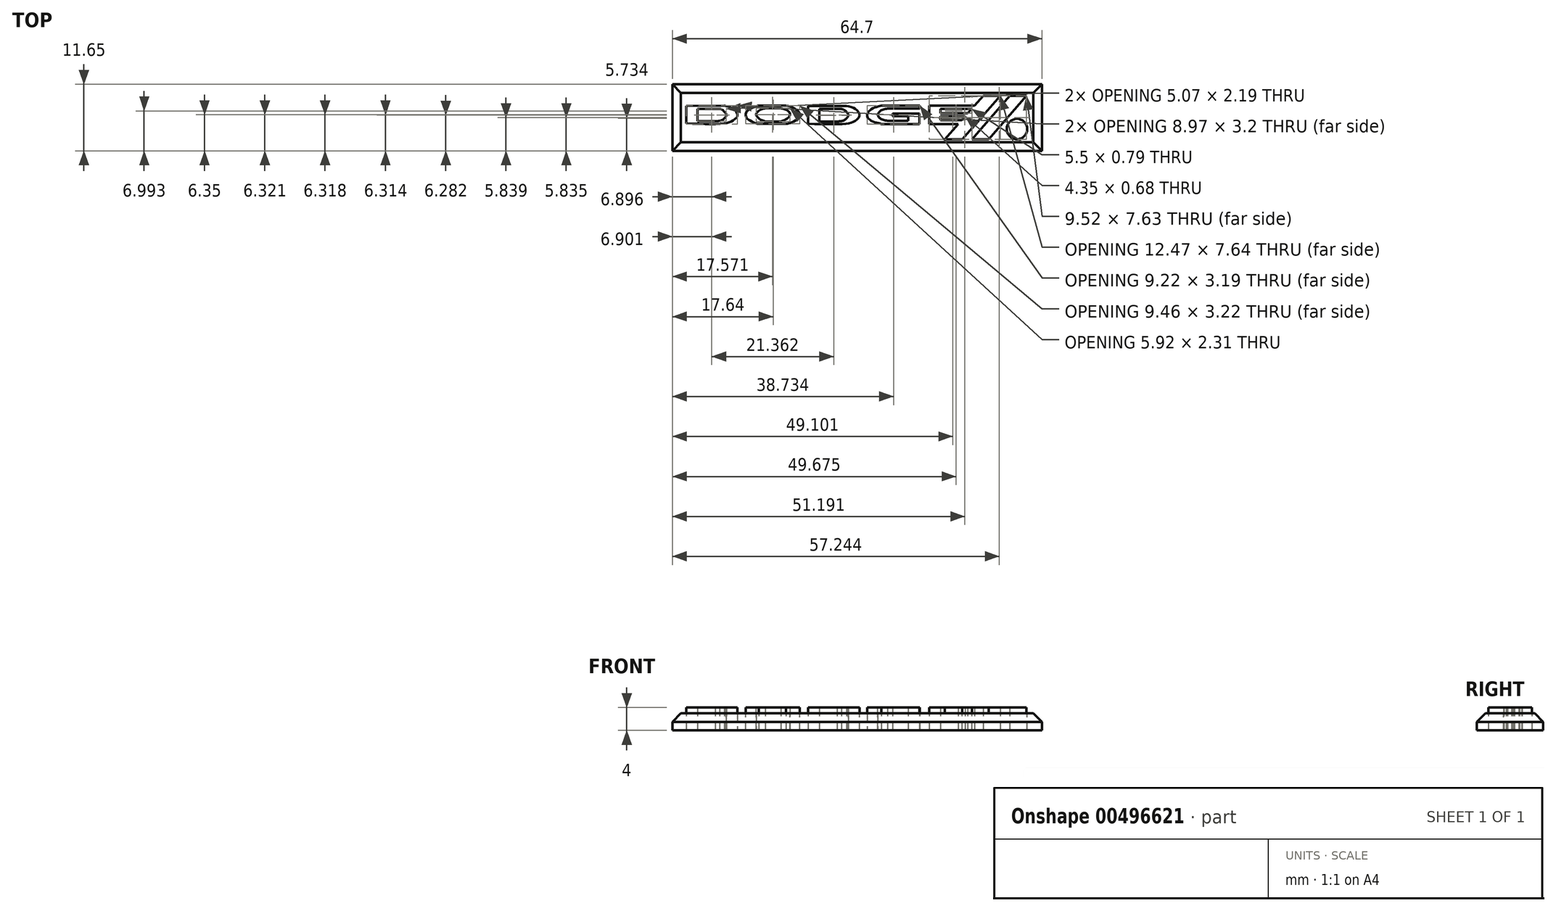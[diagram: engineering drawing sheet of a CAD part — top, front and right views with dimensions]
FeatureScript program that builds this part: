
annotation { "Feature Type Name" : "Feature", "Feature Type Description" : "" }
export const myFeature = defineFeature(function(context is Context, id is Id, definition is map)
    precondition{}
    {
        {
            var Q0;
            Q0=qCreatedBy(makeId("Top.planeOp"),FACE);
            var sketch = newSketch(context, id + "F0", { "sketchPlane" : qUnion([Q0])});
            skFitSpline(sketch, "E0", {"points": [v(0, 16.66) * mm, v(0, 13.55) * mm], "startDerivative": vector(0, -3.11) * mm, "endDerivative": vector(0, -3.11) * mm});
            skFitSpline(sketch, "E1", {"points": [v(0, 13.55) * mm, v(6.62, 13.55) * mm, v(7.96, 13.93) * mm, v(8.8, 14.55) * mm, v(8.99, 15.03) * mm, v(8.8, 15.64) * mm, v(7.95, 16.33) * mm, v(6.72, 16.67) * mm], "startDerivative": vector(26.01, -0.73) * mm, "endDerivative": vector(-9.52, 1.84) * mm});
            skFitSpline(sketch, "E2", {"points": [v(0, 16.66) * mm, v(6.72, 16.67) * mm], "startDerivative": vector(6.72, 0.01) * mm, "endDerivative": vector(6.72, 0.01) * mm});
            skFitSpline(sketch, "E3", {"points": [v(7.03, 15.1) * mm, v(7.03, 14.9) * mm, v(6.86, 14.67) * mm, v(6.62, 14.4) * mm, v(6.26, 14.16) * mm, v(5.72, 14) * mm, v(5.07, 13.95) * mm], "startDerivative": vector(0.28, -1.77) * mm, "endDerivative": vector(-3.12, -0.14) * mm});
            skFitSpline(sketch, "E4", {"points": [v(5.07, 13.95) * mm, v(1.96, 13.95) * mm], "startDerivative": vector(-3.11, 0) * mm, "endDerivative": vector(-3.11, 0) * mm});
            skFitSpline(sketch, "E5", {"points": [v(1.96, 13.95) * mm, v(1.96, 16.14) * mm], "startDerivative": vector(0, 2.2) * mm, "endDerivative": vector(0, 2.2) * mm});
            skFitSpline(sketch, "E6", {"points": [v(1.96, 16.14) * mm, v(5.86, 16.14) * mm], "startDerivative": vector(3.71, 0) * mm, "endDerivative": vector(3.71, 0) * mm});
            skFitSpline(sketch, "E7", {"points": [v(7.03, 15.1) * mm, v(7.03, 15.22) * mm, v(6.85, 15.48) * mm, v(6.52, 15.82) * mm, v(6.27, 16.01) * mm, v(5.86, 16.14) * mm], "startDerivative": vector(0.15, 0.9) * mm, "endDerivative": vector(-1.9, 0.46) * mm});
            skFitSpline(sketch, "E8", {"points": [v(15.1, 16.23) * mm, v(16.58, 16.22) * mm], "startDerivative": vector(1.48, 0) * mm, "endDerivative": vector(1.48, 0) * mm});
            skFitSpline(sketch, "E9", {"points": [v(16.58, 16.22) * mm, v(16.93, 16.15) * mm, v(17.61, 15.92) * mm, v(18.12, 15.42) * mm, v(18.19, 15.1) * mm, v(18.1, 14.87) * mm, v(17.67, 14.41) * mm, v(16.93, 14.06) * mm, v(16.58, 13.92) * mm], "startDerivative": vector(3.04, -0.61) * mm, "endDerivative": vector(-2.9, -1.12) * mm});
            skFitSpline(sketch, "E10", {"points": [v(15.1, 16.23) * mm, v(13.89, 16.23) * mm], "startDerivative": vector(-1.2, 0) * mm, "endDerivative": vector(-1.2, 0) * mm});
            skFitSpline(sketch, "E11", {"points": [v(13.89, 16.23) * mm, v(13.5, 16.14) * mm, v(12.9, 15.92) * mm, v(12.39, 15.49) * mm, v(12.27, 15.17) * mm, v(12.4, 14.83) * mm, v(12.88, 14.35) * mm, v(13.47, 14.07) * mm, v(13.89, 13.92) * mm], "startDerivative": vector(-3.28, -0.73) * mm, "endDerivative": vector(3.41, -1.16) * mm});
            skFitSpline(sketch, "E12", {"points": [v(13.89, 13.92) * mm, v(16.58, 13.92) * mm], "startDerivative": vector(2.69, 0) * mm, "endDerivative": vector(2.69, 0) * mm});
            skFitSpline(sketch, "E13", {"points": [v(15.1, 16.72) * mm, v(17.5, 16.72) * mm], "startDerivative": vector(2.4, 0) * mm, "endDerivative": vector(2.4, 0) * mm});
            skFitSpline(sketch, "E14", {"points": [v(15.1, 16.72) * mm, v(12.72, 16.72) * mm], "startDerivative": vector(-2.37, 0) * mm, "endDerivative": vector(-2.37, 0) * mm});
            skFitSpline(sketch, "E15", {"points": [v(12.72, 16.72) * mm, v(12.32, 16.6) * mm, v(11.57, 16.27) * mm, v(10.82, 15.85) * mm, v(10.5, 15.47) * mm, v(10.43, 15.12) * mm, v(10.5, 14.68) * mm, v(10.8, 14.33) * mm, v(11.63, 13.86) * mm, v(12.24, 13.56) * mm, v(12.72, 13.5) * mm], "startDerivative": vector(-4.36, -1.24) * mm, "endDerivative": vector(5.25, -0.25) * mm});
            skFitSpline(sketch, "E16", {"points": [v(12.72, 13.5) * mm, v(17.5, 13.5) * mm], "startDerivative": vector(4.78, 0) * mm, "endDerivative": vector(4.78, 0) * mm});
            skFitSpline(sketch, "E17", {"points": [v(17.5, 13.5) * mm, v(18.03, 13.6) * mm, v(19.02, 14) * mm, v(19.72, 14.5) * mm, v(19.87, 14.82) * mm, v(19.9, 15.1) * mm, v(19.85, 15.43) * mm, v(19.38, 15.92) * mm, v(18.58, 16.4) * mm, v(17.5, 16.72) * mm], "startDerivative": vector(4.78, 0.65) * mm, "endDerivative": vector(-7.66, 1.93) * mm});
            skFitSpline(sketch, "E18", {"points": [v(21.36, 16.62) * mm, v(21.36, 13.51) * mm], "startDerivative": vector(0, -3.11) * mm, "endDerivative": vector(0, -3.11) * mm});
            skFitSpline(sketch, "E19", {"points": [v(21.36, 13.51) * mm, v(27.98, 13.51) * mm, v(29.32, 13.9) * mm, v(30.16, 14.52) * mm, v(30.35, 14.99) * mm, v(30.16, 15.6) * mm, v(29.3, 16.3) * mm, v(28.08, 16.64) * mm], "startDerivative": vector(26.01, -0.73) * mm, "endDerivative": vector(-9.52, 1.84) * mm});
            skFitSpline(sketch, "E20", {"points": [v(21.36, 16.62) * mm, v(28.08, 16.64) * mm], "startDerivative": vector(6.72, 0.01) * mm, "endDerivative": vector(6.72, 0.01) * mm});
            skFitSpline(sketch, "E21", {"points": [v(28.39, 15.07) * mm, v(28.39, 14.86) * mm, v(28.23, 14.63) * mm, v(27.98, 14.35) * mm, v(27.62, 14.12) * mm, v(27.08, 13.96) * mm, v(26.43, 13.9) * mm], "startDerivative": vector(0.28, -1.77) * mm, "endDerivative": vector(-3.12, -0.14) * mm});
            skFitSpline(sketch, "E22", {"points": [v(26.43, 13.9) * mm, v(23.32, 13.9) * mm], "startDerivative": vector(-3.11, 0) * mm, "endDerivative": vector(-3.11, 0) * mm});
            skFitSpline(sketch, "E23", {"points": [v(23.32, 13.9) * mm, v(23.32, 16.1) * mm], "startDerivative": vector(0, 2.2) * mm, "endDerivative": vector(0, 2.2) * mm});
            skFitSpline(sketch, "E24", {"points": [v(23.32, 16.1) * mm, v(27.22, 16.1) * mm], "startDerivative": vector(3.71, 0) * mm, "endDerivative": vector(3.71, 0) * mm});
            skFitSpline(sketch, "E25", {"points": [v(28.39, 15.07) * mm, v(28.39, 15.19) * mm, v(28.22, 15.44) * mm, v(27.88, 15.78) * mm, v(27.63, 15.97) * mm, v(27.22, 16.1) * mm], "startDerivative": vector(0.15, 0.9) * mm, "endDerivative": vector(-1.9, 0.46) * mm});
            skLineSegment(sketch, "E26", {"start": v(40.93, 16.68) * mm, "end": v(40.93, 16.18) * mm});
            skLineSegment(sketch, "E27", {"start": v(40.93, 16.18) * mm, "end": v(35.24, 16.18) * mm});
            skLineSegment(sketch, "E28", {"start": v(40.93, 16.68) * mm, "end": v(34.2, 16.68) * mm});
            skLineSegment(sketch, "E29", {"start": v(40.83, 15.3) * mm, "end": v(36.13, 15.3) * mm});
            skLineSegment(sketch, "E30", {"start": v(36.13, 15.3) * mm, "end": v(36.13, 14.86) * mm});
            skLineSegment(sketch, "E31", {"start": v(36.13, 14.86) * mm, "end": v(38.87, 14.86) * mm});
            skLineSegment(sketch, "E32", {"start": v(38.87, 14.86) * mm, "end": v(38.87, 14.04) * mm});
            skLineSegment(sketch, "E33", {"start": v(38.87, 14.04) * mm, "end": v(35.24, 14.04) * mm});
            skLineSegment(sketch, "E34", {"start": v(40.83, 15.3) * mm, "end": v(40.83, 13.49) * mm});
            skLineSegment(sketch, "E35", {"start": v(40.83, 13.49) * mm, "end": v(34.2, 13.49) * mm});
            skFitSpline(sketch, "E36", {"points": [v(34.2, 16.68) * mm, v(33.56, 16.52) * mm, v(32.63, 16.2) * mm, v(32.05, 15.75) * mm, v(31.81, 15.45) * mm, v(31.72, 14.94) * mm, v(31.83, 14.5) * mm, v(32.06, 14.29) * mm, v(32.6, 13.96) * mm, v(33.5, 13.66) * mm, v(34.2, 13.49) * mm], "startDerivative": vector(-5.75, -1.34) * mm, "endDerivative": vector(6.13, -1.5) * mm});
            skFitSpline(sketch, "E37", {"points": [v(35.24, 16.18) * mm, v(34.7, 16.07) * mm, v(34.09, 15.82) * mm, v(33.78, 15.53) * mm, v(33.56, 15.07) * mm, v(33.8, 14.64) * mm, v(34.12, 14.37) * mm, v(34.7, 14.13) * mm, v(35.24, 14.04) * mm], "startDerivative": vector(-4.06, -0.7) * mm, "endDerivative": vector(4.08, -0.4) * mm});
            skLineSegment(sketch, "E38", {"start": v(42.55, 16.7) * mm, "end": v(42.55, 13.43) * mm});
            skLineSegment(sketch, "E39", {"start": v(42.55, 13.43) * mm, "end": v(47.49, 13.43) * mm});
            skLineSegment(sketch, "E40", {"start": v(50.3, 16.7) * mm, "end": v(42.55, 16.7) * mm});
            skLineSegment(sketch, "E41", {"start": v(44.52, 16) * mm, "end": v(44.52, 15.36) * mm});
            skLineSegment(sketch, "E42", {"start": v(44.52, 15.36) * mm, "end": v(49.04, 15.36) * mm});
            skLineSegment(sketch, "E43", {"start": v(44.52, 16) * mm, "end": v(44.52, 16.15) * mm});
            skLineSegment(sketch, "E44", {"start": v(44.52, 16.15) * mm, "end": v(49.83, 16.15) * mm});
            skLineSegment(sketch, "E45", {"start": v(48.5, 14.83) * mm, "end": v(44.52, 14.83) * mm});
            skLineSegment(sketch, "E46", {"start": v(44.52, 14.83) * mm, "end": v(44.52, 14.15) * mm});
            skLineSegment(sketch, "E47", {"start": v(44.52, 14.15) * mm, "end": v(47.93, 14.15) * mm});
            skLineSegment(sketch, "E48", {"start": v(52, 18.42) * mm, "end": v(55.02, 18.42) * mm});
            skLineSegment(sketch, "E49", {"start": v(55.02, 18.42) * mm, "end": v(48.37, 10.78) * mm});
            skLineSegment(sketch, "E50", {"start": v(48.37, 10.78) * mm, "end": v(45.32, 10.78) * mm});
            skLineSegment(sketch, "E51", {"start": v(45.32, 10.78) * mm, "end": v(52, 18.42) * mm});
            skLineSegment(sketch, "E52", {"start": v(50.3, 16.7) * mm, "end": v(50.5, 16.7) * mm});
            skLineSegment(sketch, "E53", {"start": v(49.83, 16.15) * mm, "end": v(50.01, 16.15) * mm});
            skLineSegment(sketch, "E54", {"start": v(49.04, 15.36) * mm, "end": v(49.33, 15.36) * mm});
            skLineSegment(sketch, "E55", {"start": v(48.5, 14.83) * mm, "end": v(48.87, 14.83) * mm});
            skLineSegment(sketch, "E56", {"start": v(47.93, 14.15) * mm, "end": v(48.27, 14.15) * mm});
            skLineSegment(sketch, "E57", {"start": v(47.49, 13.43) * mm, "end": v(47.64, 13.43) * mm});
            skLineSegment(sketch, "E58", {"start": v(56.65, 18.41) * mm, "end": v(59.6, 18.41) * mm});
            skLineSegment(sketch, "E59", {"start": v(59.6, 18.41) * mm, "end": v(52.96, 10.78) * mm});
            skLineSegment(sketch, "E60", {"start": v(52.96, 10.78) * mm, "end": v(50.08, 10.78) * mm});
            skLineSegment(sketch, "E61", {"start": v(50.08, 10.78) * mm, "end": v(56.65, 18.41) * mm});
            skLineSegment(sketch, "E62.bottom", {"start": v(62.29, 20.4) * mm, "end": v(-2.4, 20.4) * mm});
            skLineSegment(sketch, "E62.top", {"start": v(62.29, 8.76) * mm, "end": v(-2.4, 8.76) * mm});
            skLineSegment(sketch, "E62.left", {"start": v(62.29, 20.4) * mm, "end": v(62.29, 8.76) * mm});
            skLineSegment(sketch, "E62.right", {"start": v(-2.4, 20.4) * mm, "end": v(-2.4, 8.76) * mm});
            skSolve(sketch);
        }
        {
            var Q0;
            Q0 = qSketchRegion(id + "F0", true);
            var Q1;
            Q1=makeQuery(id+"F0.imprint","IMPRINT",FACE,{"disambiguationData":[TD([[makeQuery(id+"F0.imprint","IMPRINT",EDGE,{"derivedFrom":sQuery(id+"F0.wireOp",EDGE,"E3")}),-1.0]])]});
            var Q2;
            Q2=makeQuery(id+"F0.imprint","IMPRINT",FACE,{"disambiguationData":[TD([[makeQuery(id+"F0.imprint","IMPRINT",EDGE,{"derivedFrom":sQuery(id+"F0.wireOp",EDGE,"E8")}),-1.0]])]});
            var Q3;
            Q3=makeQuery(id+"F0.imprint","IMPRINT",FACE,{"disambiguationData":[TD([[makeQuery(id+"F0.imprint","IMPRINT",EDGE,{"derivedFrom":sQuery(id+"F0.wireOp",EDGE,"E21")}),-1.0]])]});
            var Q4;
            Q4=makeQuery(id+"F0.imprint","IMPRINT",FACE,{"disambiguationData":[TD([[makeQuery(id+"F0.imprint","IMPRINT",EDGE,{"derivedFrom":sQuery(id+"F0.wireOp",EDGE,"E45")}),1.0]])]});
            var Q5;
            Q5=makeQuery(id+"F0.imprint","IMPRINT",FACE,{"disambiguationData":[TD([[makeQuery(id+"F0.imprint","IMPRINT",EDGE,{"derivedFrom":sQuery(id+"F0.wireOp",EDGE,"E41")}),1.0]])]});
            extrude(context, id + "F1", {"entities" : qUnion([Q0, Q1, Q2, Q3, Q4, Q5]), "depth" : 3 * mm, "offsetDistance" : 25 * mm});
        }
        {
            var Q0;
            Q0=makeQuery(id+"F0.imprint","IMPRINT",FACE,{"disambiguationData":[TD([[makeQuery(id+"F0.imprint","IMPRINT",EDGE,{"derivedFrom":sQuery(id+"F0.wireOp",EDGE,"E0")}),1.0]])]});
            var Q1;
            Q1=makeQuery(id+"F0.imprint","IMPRINT",FACE,{"disambiguationData":[TD([[makeQuery(id+"F0.imprint","IMPRINT",EDGE,{"derivedFrom":sQuery(id+"F0.wireOp",EDGE,"E8")}),1.0]])]});
            var Q2;
            Q2=makeQuery(id+"F0.imprint","IMPRINT",FACE,{"disambiguationData":[TD([[makeQuery(id+"F0.imprint","IMPRINT",EDGE,{"derivedFrom":sQuery(id+"F0.wireOp",EDGE,"E18")}),1.0]])]});
            var Q3;
            Q3=makeQuery(id+"F0.imprint","IMPRINT",FACE,{"disambiguationData":[TD([[makeQuery(id+"F0.imprint","IMPRINT",EDGE,{"derivedFrom":sQuery(id+"F0.wireOp",EDGE,"E26")}),-1.0]])]});
            var Q4;
            Q4=makeQuery(id+"F0.imprint","IMPRINT",FACE,{"disambiguationData":[TD([[makeQuery(id+"F0.imprint","IMPRINT",EDGE,{"derivedFrom":sQuery(id+"F0.wireOp",EDGE,"E38")}),1.0]])]});
            var Q5;
            {var subQ3=sQuery(id+"F0.wireOp",EDGE,"E48");Q5=makeQuery(id+"F0.imprint","IMPRINT",FACE,{"disambiguationData":[TD([[makeQuery(id+"F0.imprint","IMPRINT",EDGE,{"derivedFrom":subQ3}),-1.0]])]});}
            var Q6;
            Q6=makeQuery(id+"F0.imprint","IMPRINT",FACE,{"disambiguationData":[TD([[makeQuery(id+"F0.imprint","IMPRINT",EDGE,{"derivedFrom":sQuery(id+"F0.wireOp",EDGE,"E58")}),-1.0]])]});
            extrude(context, id + "F2", {"entities" : qUnion([Q0, Q1, Q2, Q3, Q4, Q5, Q6]), "depth" : 4 * mm, "offsetDistance" : 25 * mm});
        }
        {
            var Q0;
            Q0=makeQuery(id+"F1.opExtrude","CAP_EDGE",EDGE,{"disambiguationData":[OSD([sQuery(id+"F0.wireOp",EDGE,"E62.bottom")])],"isStart":false});
            var Q1;
            Q1=makeQuery(id+"F1.opExtrude","CAP_EDGE",EDGE,{"disambiguationData":[OSD([sQuery(id+"F0.wireOp",EDGE,"E62.left")])],"isStart":false});
            var Q2;
            Q2=makeQuery(id+"F1.opExtrude","CAP_EDGE",EDGE,{"disambiguationData":[OSD([sQuery(id+"F0.wireOp",EDGE,"E62.top")])],"isStart":false});
            var Q3;
            Q3=makeQuery(id+"F1.opExtrude","CAP_EDGE",EDGE,{"disambiguationData":[OSD([sQuery(id+"F0.wireOp",EDGE,"E62.right")])],"isStart":false});
            chamfer(context, id + "F3", {"entities" : qUnion([Q0, Q1, Q2, Q3]), "width" : 1.5 * mm, "tangentPropagation" : true});
        }
        {
            var Q0;
            Q0=makeQuery(id+"F1.opExtrude","CAP_FACE",FACE,{"disambiguationData":[OSD([sQuery(id+"F0.wireOp",EDGE,"E0"),sQuery(id+"F0.wireOp",EDGE,"E1"),sQuery(id+"F0.wireOp",EDGE,"E2"),sQuery(id+"F0.wireOp",EDGE,"E13"),sQuery(id+"F0.wireOp",EDGE,"E14"),sQuery(id+"F0.wireOp",EDGE,"E15"),sQuery(id+"F0.wireOp",EDGE,"E16"),sQuery(id+"F0.wireOp",EDGE,"E17"),sQuery(id+"F0.wireOp",EDGE,"E18"),sQuery(id+"F0.wireOp",EDGE,"E19"),sQuery(id+"F0.wireOp",EDGE,"E20"),sQuery(id+"F0.wireOp",EDGE,"E26"),sQuery(id+"F0.wireOp",EDGE,"E27"),sQuery(id+"F0.wireOp",EDGE,"E28"),sQuery(id+"F0.wireOp",EDGE,"E29"),sQuery(id+"F0.wireOp",EDGE,"E30"),sQuery(id+"F0.wireOp",EDGE,"E31"),sQuery(id+"F0.wireOp",EDGE,"E32"),sQuery(id+"F0.wireOp",EDGE,"E33"),sQuery(id+"F0.wireOp",EDGE,"E34"),sQuery(id+"F0.wireOp",EDGE,"E35"),sQuery(id+"F0.wireOp",EDGE,"E36"),sQuery(id+"F0.wireOp",EDGE,"E37"),sQuery(id+"F0.wireOp",EDGE,"E38"),sQuery(id+"F0.wireOp",EDGE,"E39"),sQuery(id+"F0.wireOp",EDGE,"E40"),sQuery(id+"F0.wireOp",EDGE,"E48"),sQuery(id+"F0.wireOp",EDGE,"E49"),sQuery(id+"F0.wireOp",EDGE,"E50"),sQuery(id+"F0.wireOp",EDGE,"E51"),sQuery(id+"F0.wireOp",EDGE,"E52"),sQuery(id+"F0.wireOp",EDGE,"E57"),sQuery(id+"F0.wireOp",EDGE,"E58"),sQuery(id+"F0.wireOp",EDGE,"E59"),sQuery(id+"F0.wireOp",EDGE,"E60"),sQuery(id+"F0.wireOp",EDGE,"E61"),sQuery(id+"F0.wireOp",EDGE,"E62.bottom"),sQuery(id+"F0.wireOp",EDGE,"E62.top"),sQuery(id+"F0.wireOp",EDGE,"E62.left"),sQuery(id+"F0.wireOp",EDGE,"E62.right")])],"isStart":false});
            var sketch = newSketch(context, id + "F4", { "sketchPlane" : qUnion([Q0])});
            skCircle(sketch, "E63", {"center": v(57.94, 12.6) * mm, "radius": 1.8 * mm});
            skSolve(sketch);
        }
        {
            var Q0;
            Q0=makeQuery(id+"F4.imprint","IMPRINT",FACE,{"disambiguationData":[TD([[makeQuery(id+"F4.imprint","IMPRINT",EDGE,{"derivedFrom":sQuery(id+"F4.wireOp",EDGE,"E63")}),1.0]])]});
            extrude(context, id + "F5", {"entities" : qUnion([Q0]), "operationType" : NewBodyOperationType.REMOVE, "oppositeDirection" : true, "depth" : 3 * mm, "offsetDistance" : 25 * mm});
        }
    });
